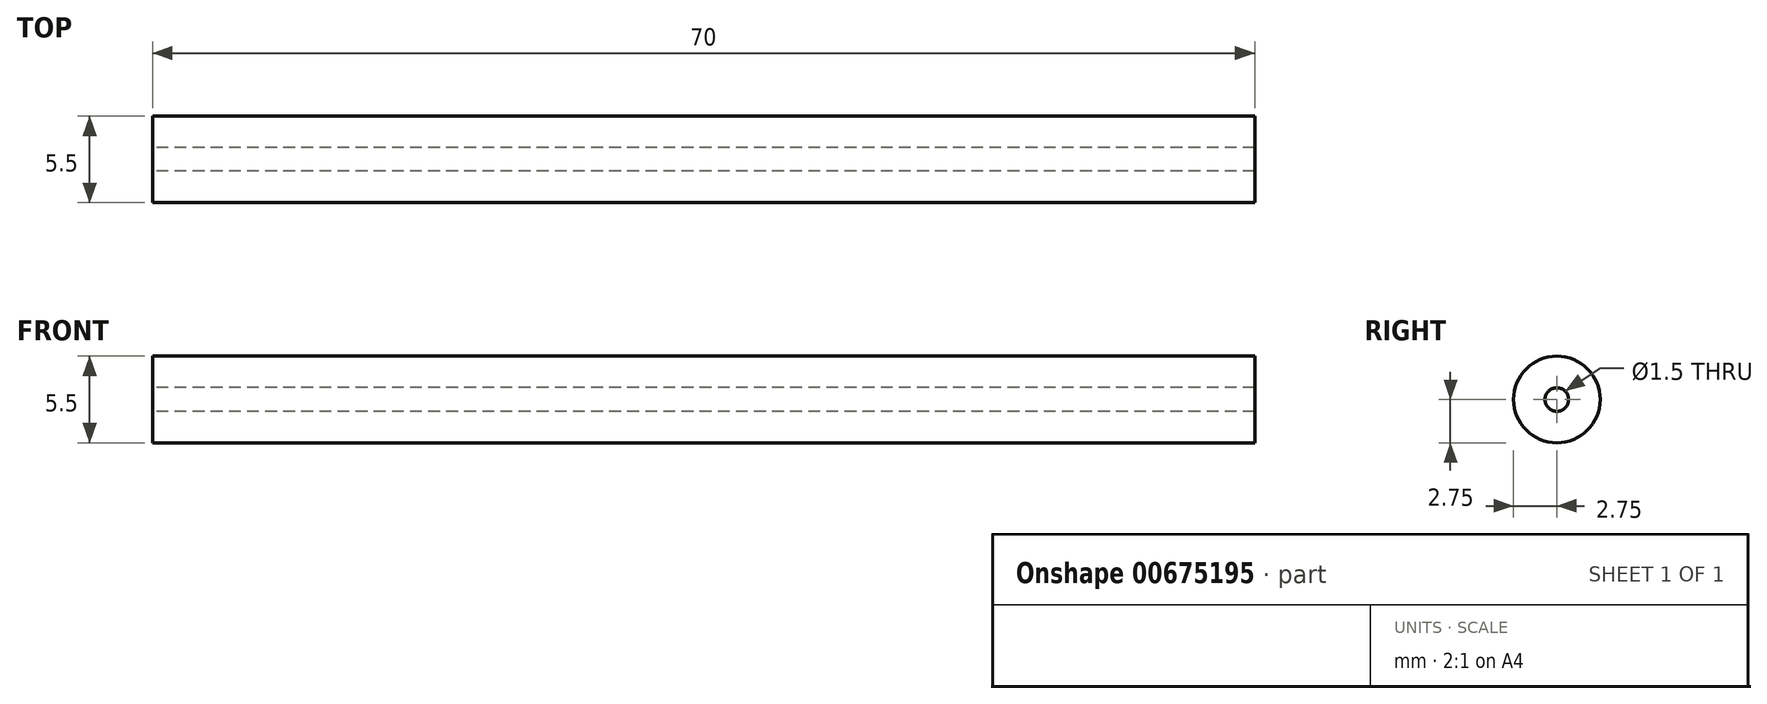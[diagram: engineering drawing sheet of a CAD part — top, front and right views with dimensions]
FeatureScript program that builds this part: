
annotation { "Feature Type Name" : "Feature", "Feature Type Description" : "" }
export const myFeature = defineFeature(function(context is Context, id is Id, definition is map)
    precondition{}
    {
        {
            var Q0;
            Q0=qCreatedBy(makeId("Right.planeOp"),FACE);
            var sketch = newSketch(context, id + "F0", { "sketchPlane" : qUnion([Q0])});
            skCircle(sketch, "E0", {"center": v(0, 0) * mm, "radius": 2.75 * mm});
            skCircle(sketch, "E1", {"center": v(0, 0) * mm, "radius": 0.75 * mm});
            skSolve(sketch);
        }
        {
            var Q0;
            Q0 = qSketchRegion(id + "F0", true);
            extrude(context, id + "F1", {"entities" : qUnion([Q0]), "depth" : 70 * mm, "offsetDistance" : 25 * mm});
        }
    });
